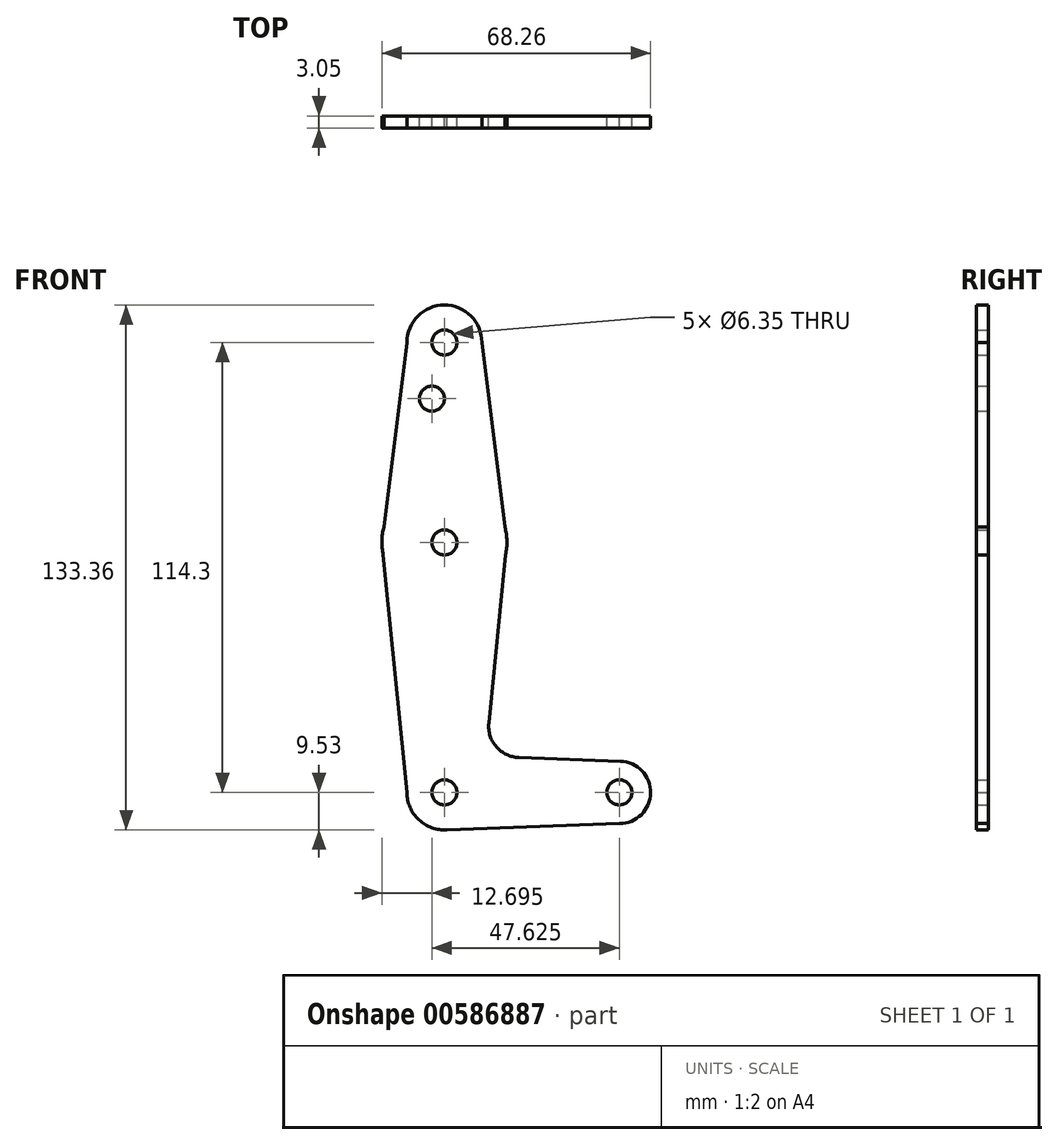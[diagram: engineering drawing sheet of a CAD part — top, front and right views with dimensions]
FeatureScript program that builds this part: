
annotation { "Feature Type Name" : "Feature", "Feature Type Description" : "" }
export const myFeature = defineFeature(function(context is Context, id is Id, definition is map)
    precondition{}
    {
        {
            var Q0;
            Q0=qCreatedBy(makeId("Front.planeOp"),FACE);
            var sketch = newSketch(context, id + "F0", { "sketchPlane" : qUnion([Q0])});
            skLineSegment(sketch, "E0", {"start": v(0, 114.3) * mm, "end": v(0, 63.5) * mm, "construction": true});
            skLineSegment(sketch, "E1", {"start": v(0, 63.5) * mm, "end": v(0, 0) * mm, "construction": true});
            skLineSegment(sketch, "E2", {"start": v(0, 0) * mm, "end": v(44.45, 0) * mm, "construction": true});
            skCircle(sketch, "E3", {"center": v(0, 114.3) * mm, "radius": 9.53 * mm});
            skCircle(sketch, "E4", {"center": v(0, 63.5) * mm, "radius": 15.88 * mm});
            skCircle(sketch, "E5", {"center": v(0, 0) * mm, "radius": 9.53 * mm});
            skCircle(sketch, "E6", {"center": v(44.45, 0) * mm, "radius": 7.94 * mm});
            skLineSegment(sketch, "E7", {"start": v(18.91, 8.85) * mm, "end": v(44.73, 7.93) * mm});
            skLineSegment(sketch, "E8", {"start": v(0, -9.52) * mm, "end": v(44.45, -7.94) * mm});
            skLineSegment(sketch, "E9", {"start": v(-9.53, 114.3) * mm, "end": v(-15.88, 63.5) * mm});
            skLineSegment(sketch, "E10", {"start": v(-15.88, 63.5) * mm, "end": v(-9.52, 0) * mm});
            skLineSegment(sketch, "E11", {"start": v(11.28, 17.59) * mm, "end": v(15.87, 63.5) * mm});
            skLineSegment(sketch, "E12", {"start": v(15.87, 63.5) * mm, "end": v(9.52, 114.3) * mm});
            skCircle(sketch, "E13", {"center": v(0, 114.3) * mm, "radius": 3.18 * mm});
            skCircle(sketch, "E14", {"center": v(0, 63.5) * mm, "radius": 3.18 * mm});
            skCircle(sketch, "E15", {"center": v(0, 0) * mm, "radius": 3.18 * mm});
            skCircle(sketch, "E16", {"center": v(44.45, 0) * mm, "radius": 3.18 * mm});
            skCircle(sketch, "E17", {"center": v(-3.17, 100.03) * mm, "radius": 3.18 * mm});
            skArc(sketch, "E18.filletArc", {"start": v(11.28, 17.59) * mm, "mid": v(13.2, 11.57) * mm, "end": v(18.91, 8.85) * mm});
            skSolve(sketch);
        }
        {
            var Q0;
            Q0 = qSketchRegion(id + "F0", true);
            extrude(context, id + "F1", {"entities" : qUnion([Q0]), "depth" : 3.05 * mm, "offsetDistance" : 25.4 * mm});
        }
    });
